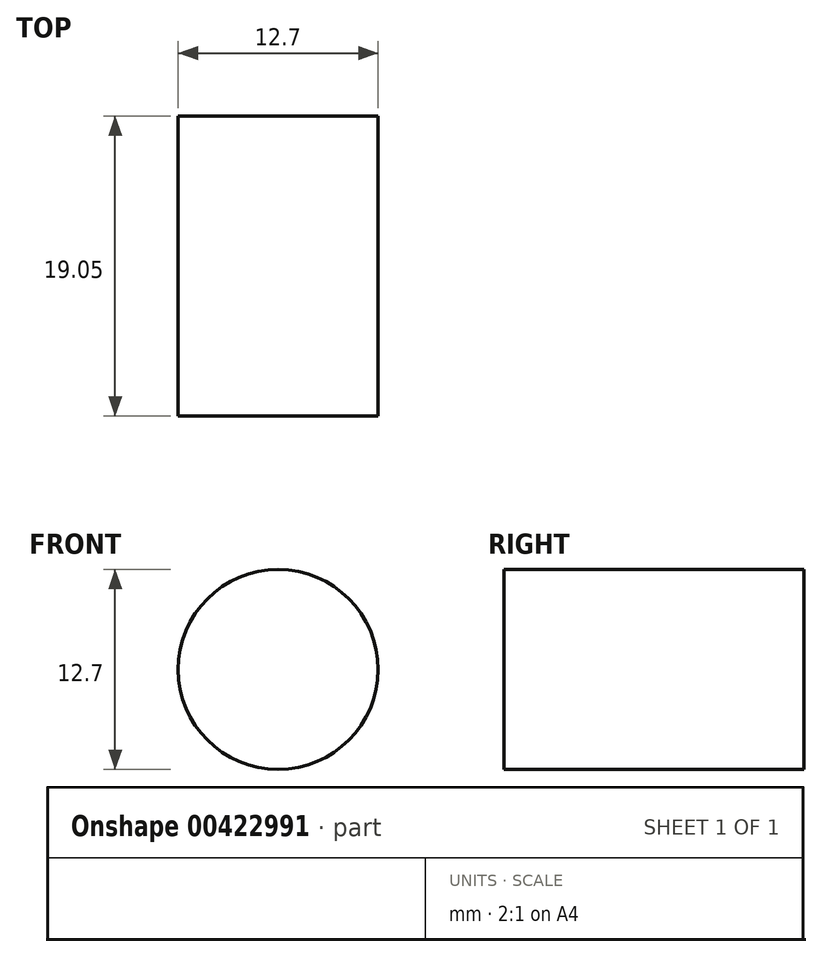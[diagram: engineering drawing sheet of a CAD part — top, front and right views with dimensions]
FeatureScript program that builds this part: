
annotation { "Feature Type Name" : "Feature", "Feature Type Description" : "" }
export const myFeature = defineFeature(function(context is Context, id is Id, definition is map)
    precondition{}
    {
        {
            var Q0;
            Q0=qCreatedBy(makeId("Front.planeOp"),FACE);
            var sketch = newSketch(context, id + "F0", { "sketchPlane" : qUnion([Q0])});
            skCircle(sketch, "E0", {"center": v(0, 0) * mm, "radius": 6.35 * mm});
            skSolve(sketch);
        }
        {
            var Q0;
            Q0 = qSketchRegion(id + "F0", true);
            extrude(context, id + "F1", {"entities" : qUnion([Q0]), "depth" : 19.05 * mm});
        }
    });
